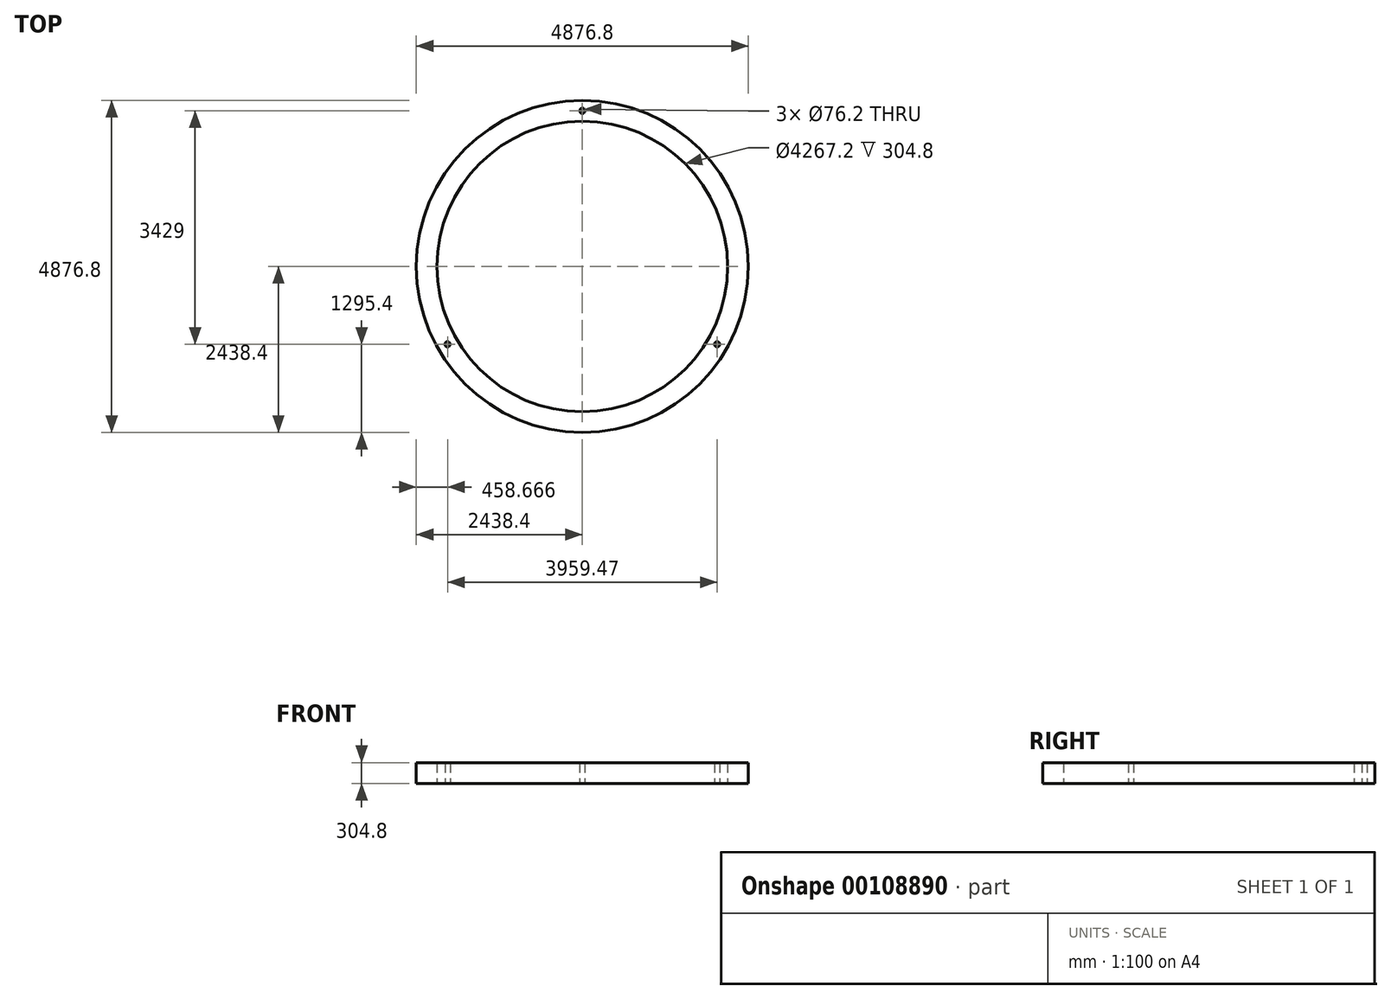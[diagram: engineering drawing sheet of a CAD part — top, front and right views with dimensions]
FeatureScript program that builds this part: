
annotation { "Feature Type Name" : "Feature", "Feature Type Description" : "" }
export const myFeature = defineFeature(function(context is Context, id is Id, definition is map)
    precondition{}
    {
        {
            var Q0;
            Q0=qCreatedBy(makeId("Top.planeOp"),FACE);
            var sketch = newSketch(context, id + "F0", { "sketchPlane" : qUnion([Q0])});
            skCircle(sketch, "E0", {"center": v(0, 0) * mm, "radius": 2438.4 * mm});
            skCircle(sketch, "E1", {"center": v(0, 0) * mm, "radius": 2133.6 * mm});
            skLineSegment(sketch, "E2", {"start": v(0, 0) * mm, "end": v(0, 3075.3) * mm, "construction": true});
            skLineSegment(sketch, "E3", {"start": v(0, 0) * mm, "end": v(-3290.6, -1899.83) * mm, "construction": true});
            skLineSegment(sketch, "E4", {"start": v(0, 0) * mm, "end": v(3281.87, -1894.79) * mm, "construction": true});
            skCircle(sketch, "E5", {"center": v(0, 0) * mm, "radius": 2286 * mm, "construction": true});
            skCircle(sketch, "E6", {"center": v(0, 2286) * mm, "radius": 38.1 * mm});
            skCircle(sketch, "E7", {"center": v(1979.73, -1143) * mm, "radius": 38.1 * mm});
            skCircle(sketch, "E8", {"center": v(-1979.73, -1143) * mm, "radius": 38.1 * mm});
            skSolve(sketch);
        }
        {
            var Q0;
            Q0 = qSketchRegion(id + "F0", true);
            var Q1;
            Q1 = qSketchRegion(id + "FIcSQ96wOO7fEqA_0", true);
            extrude(context, id + "F1", {"entities" : qUnion([Q0, Q1]), "depth" : 304.8 * mm});
        }
    });
